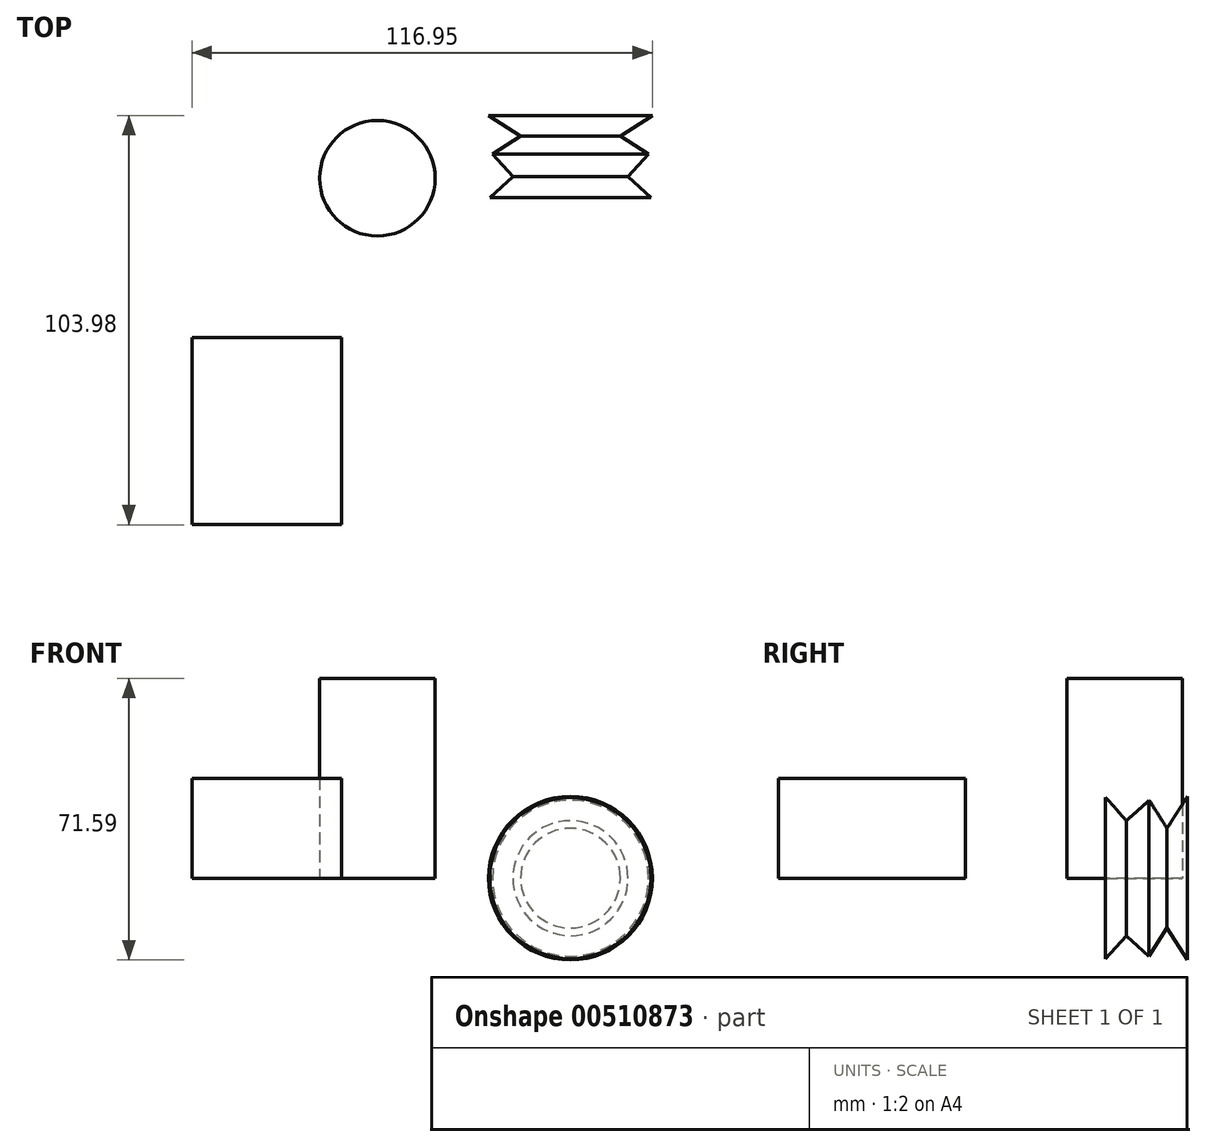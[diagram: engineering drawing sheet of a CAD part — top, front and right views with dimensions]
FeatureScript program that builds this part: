
annotation { "Feature Type Name" : "Feature", "Feature Type Description" : "" }
export const myFeature = defineFeature(function(context is Context, id is Id, definition is map)
    precondition{}
    {
        {
            var Q0;
            Q0=qCreatedBy(makeId("Top.planeOp"),FACE);
            var sketch = newSketch(context, id + "F0", { "sketchPlane" : qUnion([Q0])});
            skLineSegment(sketch, "E0", {"start": v(-66.22, 27.43) * mm, "end": v(-48.55, 47.5) * mm});
            skLineSegment(sketch, "E1", {"start": v(-48.55, 47.5) * mm, "end": v(-2.01, 37.7) * mm});
            skLineSegment(sketch, "E2.bottom", {"start": v(-66.92, 0) * mm, "end": v(-28.9, 0) * mm});
            skLineSegment(sketch, "E2.top", {"start": v(-66.92, -47.6) * mm, "end": v(-28.9, -47.6) * mm});
            skLineSegment(sketch, "E2.left", {"start": v(-66.92, 0) * mm, "end": v(-66.92, -47.6) * mm});
            skLineSegment(sketch, "E2.right", {"start": v(-28.9, 0) * mm, "end": v(-28.9, -47.6) * mm});
            skSolve(sketch);
        }
        {
            var Q0;
            Q0 = qSketchRegion(id + "F0", true);
            extrude(context, id + "F1", {"entities" : qUnion([Q0]), "depth" : 25.4 * mm});
        }
        {
            var Q0;
            Q0=qCreatedBy(makeId("Top.planeOp"),FACE);
            var sketch = newSketch(context, id + "F2", { "sketchPlane" : qUnion([Q0])});
            skCircle(sketch, "E3", {"center": v(-19.8, 40.43) * mm, "radius": 14.68 * mm});
            skSolve(sketch);
        }
        {
            var Q0;
            Q0 = qSketchRegion(id + "F2", true);
            extrude(context, id + "F3", {"entities" : qUnion([Q0]), "depth" : 50.8 * mm});
        }
        {
            var Q0;
            Q0=qCreatedBy(makeId("Top.planeOp"),FACE);
            var sketch = newSketch(context, id + "F4", { "sketchPlane" : qUnion([Q0])});
            skLineSegment(sketch, "E4", {"start": v(50.03, 56.37) * mm, "end": v(29.24, 56.37) * mm});
            skLineSegment(sketch, "E5", {"start": v(29.24, 56.37) * mm, "end": v(29.24, 35.57) * mm});
            skLineSegment(sketch, "E6", {"start": v(29.24, 35.57) * mm, "end": v(49.7, 35.57) * mm});
            skLineSegment(sketch, "E7", {"start": v(49.7, 35.57) * mm, "end": v(43.85, 40.87) * mm});
            skLineSegment(sketch, "E8", {"start": v(43.85, 40.87) * mm, "end": v(49.06, 46.62) * mm});
            skLineSegment(sketch, "E9", {"start": v(49.06, 46.62) * mm, "end": v(41.9, 51.17) * mm});
            skLineSegment(sketch, "E10", {"start": v(41.9, 51.17) * mm, "end": v(50.03, 56.37) * mm});
            skSolve(sketch);
        }
        {
            var Q0;
            Q0=makeQuery(id+"F4.imprint","IMPRINT",FACE,{"disambiguationData":[TD([[makeQuery(id+"F4.imprint","IMPRINT",EDGE,{"derivedFrom":sQuery(id+"F4.wireOp",EDGE,"E4")}),1.0]])]});
            var Q1;
            Q1=sQuery(id+"F4.wireOp",EDGE,"E5");
            revolve(context, id + "F5", {"entities" : qUnion([Q0]), "axis" : qUnion([Q1]), "revolveType" : RevolveType.FULL});
        }
    });
